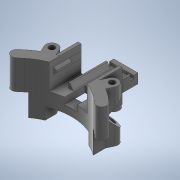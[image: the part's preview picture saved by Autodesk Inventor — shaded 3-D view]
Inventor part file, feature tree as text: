
AUTODESK INVENTOR PART (.ipt)
format: ipt  version: 2020 (Build 240168000, 168)  size: 733,184 bytes
history: native  units: mm
features: extrude x17, sketch x16, projected_geometry x14, other x5, sweep x1, chamfer x1
ambient origin geometry x8: Origin, YZ Plane, XZ Plane, XY Plane, X Axis, Y Axis, Z Axis, Center Point
bodies: Body1 (feature_tree)
feature tree (54):
  other  "Твердое тело1"
  extrude  "Выдавливание1"  Depth=35.0mm TaperAngle=0.0deg
  sketch  "Эскиз2"
  extrude  "Выдавливание2"  Depth=4.0mm
  sweep  "Сдвиг1"
  extrude  "Выдавливание5"  Depth=8.0mm
  extrude  "Выдавливание6"  Depth=35.0mm TaperAngle=0.0deg
  extrude  "Выдавливание7"  Depth=8.5mm
  extrude  "Выдавливание8"  TaperAngle=45.0deg  [1 undecoded]
  other  "РабПлоскость1"
  extrude  "Выдавливание9"  Depth=8.5mm
  extrude  "Выдавливание10"  TaperAngle=45.0deg  [1 undecoded]
  extrude  "Выдавливание11"  TaperAngle=0.0deg  [1 undecoded]
  sketch  "Эскиз13"
  other  "РабПлоскость2"
  sketch  "Эскиз14"
  extrude  "Выдавливание12"  Depth=5.0mm TaperAngle=0.0deg
  extrude  "Выдавливание13"  Depth=15.0mm TaperAngle=0.0deg
  other  "РабПлоскость3"
  extrude  "Выдавливание14"  Depth=15.0mm TaperAngle=0.0deg
  extrude  "Выдавливание15"  Depth=26.0mm
  extrude  "Выдавливание16"  Depth=6.0mm
  extrude  "Выдавливание17"  Depth=15.0mm TaperAngle=0.0deg
  chamfer  "Фаска1"  Distance=2.0mm
  other  "РабПлоскость4"
  sketch  "Эскиз18"
  extrude  "Выдавливание18"  Depth=1.5mm
  extrude  "Выдавливание19"  Depth=3.0mm
  sketch  "Эскиз1"
  sketch  "Эскиз3"
  projected_geometry  "Спроецированная петля1"
  projected_geometry  "Спроецированная петля2"
  sketch  "3D эскиз1"
  sketch  "Эскиз4"
  sketch  "Эскиз6"
  projected_geometry  "Спроецированная петля4"
  sketch  "Эскиз7"
  projected_geometry  "Спроецированная петля5"
  sketch  "Эскиз9"
  projected_geometry  "Спроецированная петля7"
  sketch  "Эскиз11"
  projected_geometry  "Спроецированная петля8"
  sketch  "Эскиз12"
  projected_geometry  "Спроецированная петля9"
  projected_geometry  "Спроецированная петля10"
  sketch  "Эскиз15"
  sketch  "Эскиз16"
  projected_geometry  "Спроецированная петля11"
  projected_geometry  "Спроецированная петля12"
  sketch  "Эскиз17"
  projected_geometry  "Спроецированная петля13"
  projected_geometry  "Спроецированная петля14"
  projected_geometry  "Спроецированная петля15"
  projected_geometry  "Спроецированная петля16"
note: 3 required parameter values undecoded (feature->parameter linkage not recoverable at this tier; creation-order binding heuristic only, values carry confidence <= 0.55)
